# Revit family: 1AFQM6_DN40-50_PN16_RFA
name_source: partatom
category: Pipe Accessories
units: mm (PartAtom-declared; Revit-internal decimal feet)

## family parameters
Always vertical = Yes
Cut with Voids When Loaded = No
OmniClass Number = 23.65.55.14.17
OmniClass Title = Adjusting/Controlling Valves for Liquid Services
Part Type = Valve - Breaks Into
Round Connector Dimension = Use Diameter
Shared = No
Work Plane-Based = No

## types (2) — shared parameters
C1 = 77 mm  [stored 0.252625 ft]
Connection = Flange
D = 40 mm  [stored 0.131234 ft]
D2 = 120 mm  [stored 0.393701 ft]
Description = Pressure Independent Control Valve
Differential Pressure over Control Valve = 0 bar
Flange_l1 = 131.872 mm
H = 645 mm  [stored 2.11614 ft]
H1 = 383 mm  [stored 1.25656 ft]
H2 = 252.5 mm  [stored 0.828412 ft]
IfcExportAs = IfcValveType
IfcExportType = AFQM6
LOD 200 = No
LOD 350 = Yes
Manufacturer = Danfoss
Max Differential Pressure = 16 bar
Max Medium Temperature = 150 °C
Min Medium Temperature = 2 °C
Nominal Pressure = PN 16
P1 = 18 mm  [stored 0.0590551 ft]
Rectangular_flange = Yes
Round_flange = No
URL = https://store.danfoss.com
Valve Body Material = Danfoss Grey Cast Iron
d1 = 100 mm  [stored 0.328084 ft]
d4 = 76 mm  [stored 0.249344 ft]
d5 = 42 mm  [stored 0.137795 ft]
f = 3 mm  [stored 0.00984252 ft]

## per-type parameters (varying)
| type | D1 | Dr1 | Impulsetube_offset | Kvs | L | Max Flow | Min Flow | Model | Model Type | R | R1 | Stroke | V | W | Weight | b1 | d1l | d2 | d3 | d4-1 | d4l | d5l | t1 |
| AFQM6_DN40_PN16_003G1082 | 146 mm  [stored 0.479003 ft] | 70 mm  [stored 0.229659 ft] | 85 mm  [stored 0.278871 ft] | 20.0 m³/h | 200 mm  [stored 0.656168 ft] | 11 m3/h | 2.2 m3/h | 003G1082 | AFQM6_DN40_PN16
AFQM2_DN65_PN16_dPcv0.2bar | 119 mm  [stored 0.39042 ft] | 68 mm | 8 mm | 91.25 mm | 318 mm  [stored 1.04331 ft] | 17.00 kg | 15 mm  [stored 0.0492126 ft] | 135.25 mm  [stored 0.443734 ft] | 48 mm  [stored 0.15748 ft] | 97 mm  [stored 0.318241 ft] | 92 mm  [stored 0.301837 ft] | 68 mm | 39.5 mm | 2.45 mm  [stored 0.00803806 ft] |
| AFQM6_DN50_PN16_003G1083 | 165 mm | 82 mm  [stored 0.269029 ft] | 100 mm  [stored 0.328084 ft] | 32.0 m³/h | 230 mm  [stored 0.754593 ft] | 16 m3/h | 3.2 m3/h | 003G1083 | AFQM6_DN50_PN16
AFQM2_DN65_PN16_dPcv0.2bar | 140 mm  [stored 0.459318 ft] | 77 mm  [stored 0.252625 ft] | 12 mm | 73 mm  [stored 0.239501 ft] | 267.5 mm  [stored 0.877625 ft] | 22.00 kg | 17 mm  [stored 0.0557743 ft] | 139 mm  [stored 0.456037 ft] | 58 mm | 104 mm | 106 mm  [stored 0.347769 ft] | 70 mm  [stored 0.229659 ft] | 37 mm  [stored 0.121391 ft] | 3 mm  [stored 0.00984252 ft] |

note: [stored X ft] marks values corroborated as IEEE doubles in the binary element streams (Revit-internal decimal feet)

## geometry (parser evidence)
native form markers: Sweep x4
no freeform markers — native parametric forms only
